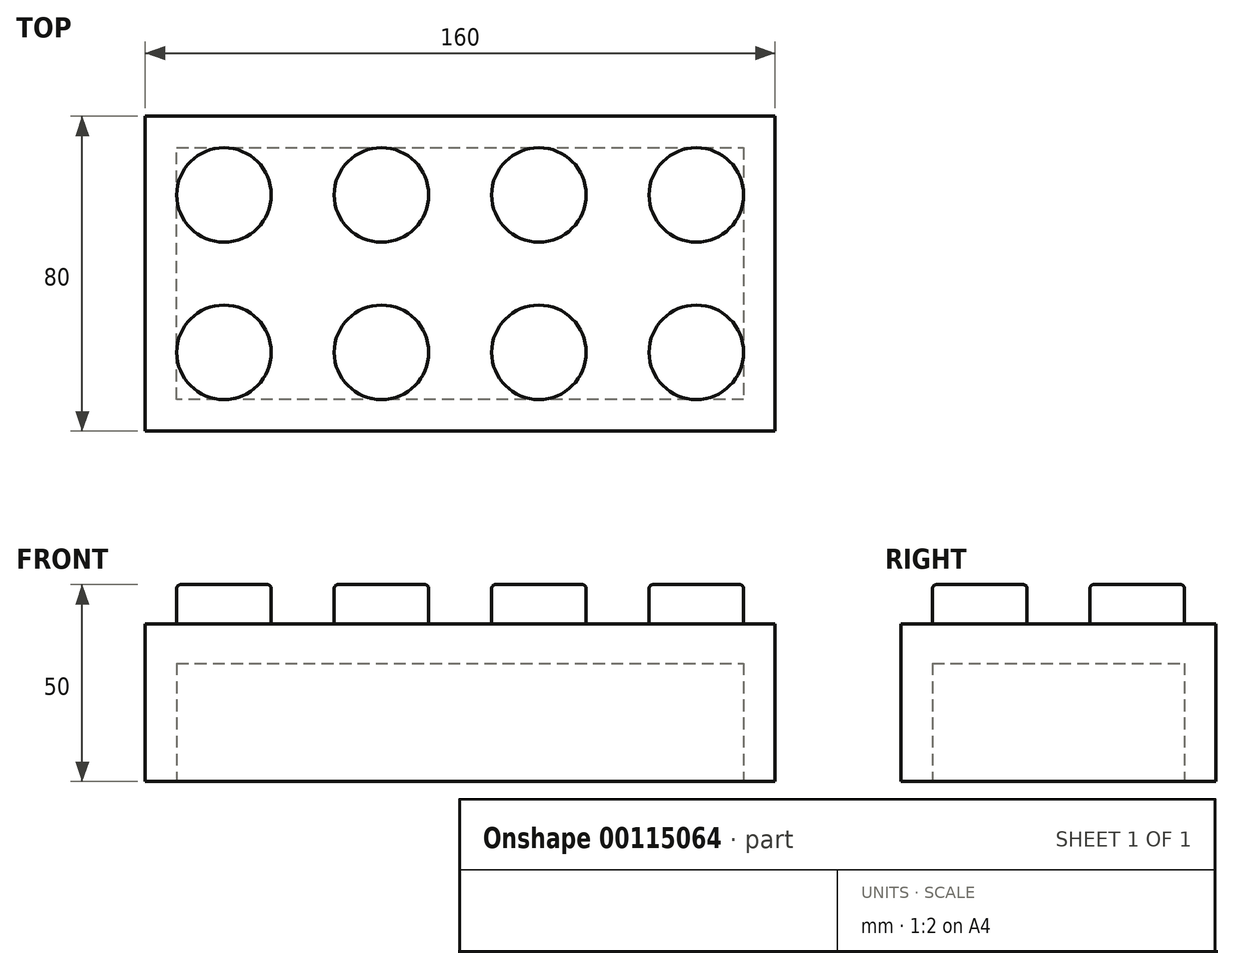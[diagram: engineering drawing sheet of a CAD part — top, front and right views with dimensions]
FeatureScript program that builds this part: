
annotation { "Feature Type Name" : "Feature", "Feature Type Description" : "" }
export const myFeature = defineFeature(function(context is Context, id is Id, definition is map)
    precondition{}
    {
        {
            var Q0;
            Q0=qCreatedBy(makeId("Top.planeOp"),FACE);
            var sketch = newSketch(context, id + "F0", { "sketchPlane" : qUnion([Q0])});
            skLineSegment(sketch, "E0.bottom", {"start": v(-88.8, 24.63) * mm, "end": v(71.2, 24.63) * mm});
            skLineSegment(sketch, "E0.top", {"start": v(-88.8, -55.37) * mm, "end": v(71.2, -55.37) * mm});
            skLineSegment(sketch, "E0.left", {"start": v(-88.8, 24.63) * mm, "end": v(-88.8, -55.37) * mm});
            skLineSegment(sketch, "E0.right", {"start": v(71.2, 24.63) * mm, "end": v(71.2, -55.37) * mm});
            skSolve(sketch);
        }
        {
            var Q0;
            Q0=makeQuery(id+"F0.imprint","IMPRINT",FACE,{"disambiguationData":[TD([[makeQuery(id+"F0.imprint","IMPRINT",EDGE,{"derivedFrom":sQuery(id+"F0.wireOp",EDGE,"E0.bottom")}),-1.0]])]});
            extrude(context, id + "F1", {"entities" : qUnion([Q0]), "depth" : 40 * mm});
        }
        {
            var Q0;
            Q0=makeQuery(id+"F1.opExtrude","CAP_FACE",FACE,{"disambiguationData":[OSD([sQuery(id+"F0.wireOp",EDGE,"E0.bottom"),sQuery(id+"F0.wireOp",EDGE,"E0.top"),sQuery(id+"F0.wireOp",EDGE,"E0.left"),sQuery(id+"F0.wireOp",EDGE,"E0.right")])],"isStart":true});
            var sketch = newSketch(context, id + "F2", { "sketchPlane" : qUnion([Q0])});
            skLineSegment(sketch, "E1.0", {"start": v(-80.8, -16.63) * mm, "end": v(63.2, -16.63) * mm});
            skLineSegment(sketch, "E1.1", {"start": v(-80.8, 47.37) * mm, "end": v(-80.8, -16.63) * mm});
            skLineSegment(sketch, "E1.2", {"start": v(63.2, 47.37) * mm, "end": v(-80.8, 47.37) * mm});
            skLineSegment(sketch, "E1.3", {"start": v(63.2, -16.63) * mm, "end": v(63.2, 47.37) * mm});
            skSolve(sketch);
        }
        {
            var Q0;
            Q0=makeQuery(id+"F2.imprint","IMPRINT",FACE,{"disambiguationData":[TD([[makeQuery(id+"F2.imprint","IMPRINT",EDGE,{"derivedFrom":sQuery(id+"F2.wireOp",EDGE,"E1.0")}),1.0]])]});
            extrude(context, id + "F3", {"entities" : qUnion([Q0]), "operationType" : NewBodyOperationType.REMOVE, "oppositeDirection" : true, "depth" : 30 * mm});
        }
        {
            var Q0;
            Q0=makeQuery(id+"F1.opExtrude","CAP_FACE",FACE,{"disambiguationData":[OSD([sQuery(id+"F0.wireOp",EDGE,"E0.bottom"),sQuery(id+"F0.wireOp",EDGE,"E0.top"),sQuery(id+"F0.wireOp",EDGE,"E0.left"),sQuery(id+"F0.wireOp",EDGE,"E0.right")])],"isStart":false});
            var sketch = newSketch(context, id + "F4", { "sketchPlane" : qUnion([Q0])});
            skCircle(sketch, "E2", {"center": v(-68.8, 4.63) * mm, "radius": 12 * mm});
            skCircle(sketch, "E3.0.1.0", {"center": v(-68.8, -35.37) * mm, "radius": 12 * mm});
            skCircle(sketch, "E3.1.0.0", {"center": v(-28.8, 4.63) * mm, "radius": 12 * mm});
            skCircle(sketch, "E3.1.1.0", {"center": v(-28.8, -35.37) * mm, "radius": 12 * mm});
            skCircle(sketch, "E3.2.0.0", {"center": v(11.2, 4.63) * mm, "radius": 12 * mm});
            skCircle(sketch, "E3.2.1.0", {"center": v(11.2, -35.37) * mm, "radius": 12 * mm});
            skCircle(sketch, "E3.3.0.0", {"center": v(51.2, 4.63) * mm, "radius": 12 * mm});
            skCircle(sketch, "E3.3.1.0", {"center": v(51.2, -35.37) * mm, "radius": 12 * mm});
            skLineSegment(sketch, "E3.direction1", {"start": v(-68.8, 4.63) * mm, "end": v(-28.8, 4.63) * mm, "construction": true});
            skLineSegment(sketch, "E3.direction2", {"start": v(-68.8, 4.63) * mm, "end": v(-68.8, -35.37) * mm, "construction": true});
            skSolve(sketch);
        }
        {
            var Q0;
            Q0 = qSketchRegion(id + "F4", true);
            extrude(context, id + "F5", {"entities" : qUnion([Q0]), "operationType" : NewBodyOperationType.ADD, "depth" : 10 * mm});
        }
        {
            var Q0;
            Q0=makeQuery(id+"F5.opExtrude","CAP_FACE",FACE,{"disambiguationData":[OSD([sQuery(id+"F4.wireOp",EDGE,"E2")])],"isStart":false});
            var Q1;
            Q1=makeQuery(id+"F5.opExtrude","CAP_FACE",FACE,{"disambiguationData":[OSD([sQuery(id+"F4.wireOp",EDGE,"E3.1.0.0")])],"isStart":false});
            var Q2;
            Q2=makeQuery(id+"F5.opExtrude","CAP_FACE",FACE,{"disambiguationData":[OSD([sQuery(id+"F4.wireOp",EDGE,"E3.2.0.0")])],"isStart":false});
            var Q3;
            Q3=makeQuery(id+"F5.opExtrude","CAP_FACE",FACE,{"disambiguationData":[OSD([sQuery(id+"F4.wireOp",EDGE,"E3.3.0.0")])],"isStart":false});
            var Q4;
            Q4=makeQuery(id+"F5.opExtrude","CAP_FACE",FACE,{"disambiguationData":[OSD([sQuery(id+"F4.wireOp",EDGE,"E3.3.1.0")])],"isStart":false});
            var Q5;
            Q5=makeQuery(id+"F5.opExtrude","CAP_FACE",FACE,{"disambiguationData":[OSD([sQuery(id+"F4.wireOp",EDGE,"E3.2.1.0")])],"isStart":false});
            var Q6;
            Q6=makeQuery(id+"F5.opExtrude","CAP_FACE",FACE,{"disambiguationData":[OSD([sQuery(id+"F4.wireOp",EDGE,"E3.1.1.0")])],"isStart":false});
            var Q7;
            Q7=makeQuery(id+"F5.opExtrude","CAP_FACE",FACE,{"disambiguationData":[OSD([sQuery(id+"F4.wireOp",EDGE,"E3.0.1.0")])],"isStart":false});
            fillet(context, id + "F6", {"entities" : qUnion([Q0, Q1, Q2, Q3, Q4, Q5, Q6, Q7]), "radius" : 1 * mm, "tangentPropagation" : true, "allowEdgeOverflow" : false});
        }
    });
